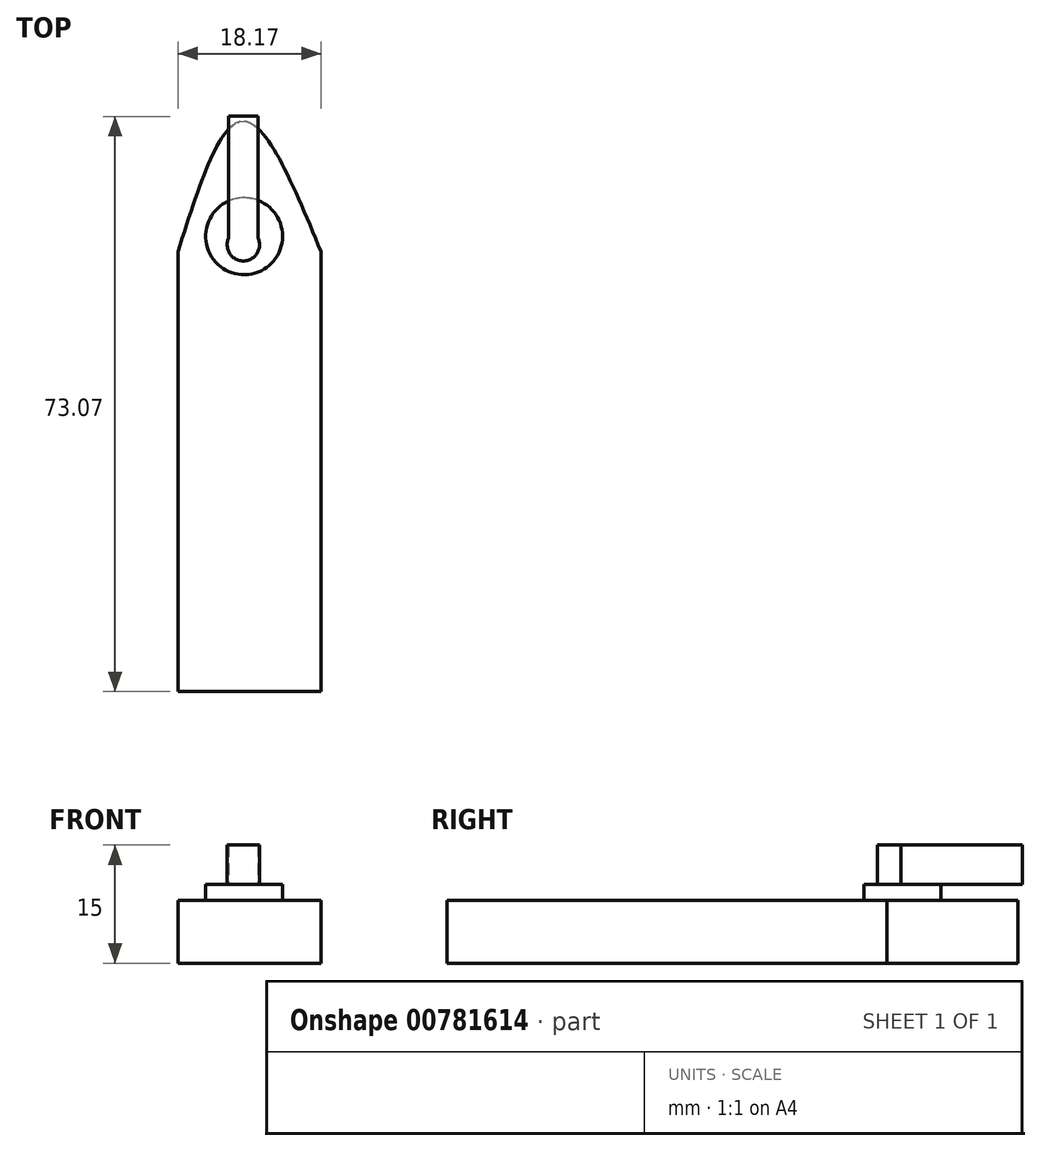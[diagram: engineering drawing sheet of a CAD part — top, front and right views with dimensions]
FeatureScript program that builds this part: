
annotation { "Feature Type Name" : "Feature", "Feature Type Description" : "" }
export const myFeature = defineFeature(function(context is Context, id is Id, definition is map)
    precondition{}
    {
        {
            var Q0;
            Q0=qCreatedBy(makeId("Top.planeOp"),FACE);
            var sketch = newSketch(context, id + "F0", { "sketchPlane" : qUnion([Q0])});
            skLineSegment(sketch, "E0", {"start": v(-36.83, -32.63) * mm, "end": v(-36.83, 23.25) * mm});
            skLineSegment(sketch, "E1", {"start": v(-36.83, 23.25) * mm, "end": v(-18.66, 23.25) * mm});
            skLineSegment(sketch, "E2", {"start": v(-18.66, 23.25) * mm, "end": v(-18.66, -32.63) * mm});
            skLineSegment(sketch, "E3", {"start": v(-18.66, -32.63) * mm, "end": v(-36.83, -32.63) * mm});
            skFitSpline(sketch, "E4", {"points": [v(-36.83, 23.25) * mm, v(-28.62, 39.86) * mm, v(-18.66, 23.25) * mm], "startDerivative": vector(15.83, 50.01) * mm, "endDerivative": vector(20.5, -49.64) * mm});
            skSolve(sketch);
        }
        {
            var Q0;
            Q0 = qSketchRegion(id + "F0", true);
            extrude(context, id + "F1", {"entities" : qUnion([Q0]), "depth" : 8 * mm, "offsetDistance" : 25.4 * mm});
        }
        {
            var Q0;
            Q0=makeQuery(id+"F1.opExtrude","CAP_FACE",FACE,{"disambiguationData":[OSD([sQuery(id+"F0.wireOp",EDGE,"E0"),sQuery(id+"F0.wireOp",EDGE,"E2"),sQuery(id+"F0.wireOp",EDGE,"E3"),sQuery(id+"F0.wireOp",EDGE,"E4")])],"isStart":false});
            var sketch = newSketch(context, id + "F2", { "sketchPlane" : qUnion([Q0])});
            skCircle(sketch, "E5", {"center": v(-28.43, 25.2) * mm, "radius": 4.89 * mm});
            skSolve(sketch);
        }
        {
            var Q0;
            Q0=makeQuery(id+"F2.imprint","IMPRINT",FACE,{"disambiguationData":[TD([[makeQuery(id+"F2.imprint","IMPRINT",EDGE,{"derivedFrom":sQuery(id+"F2.wireOp",EDGE,"E5")}),1.0]])]});
            extrude(context, id + "F3", {"entities" : qUnion([Q0]), "operationType" : NewBodyOperationType.ADD, "depth" : 2 * mm, "offsetDistance" : 25.4 * mm});
        }
        {
            var Q0;
            Q0=makeQuery(id+"F3.opExtrude","CAP_FACE",FACE,{"disambiguationData":[OSD([sQuery(id+"F2.wireOp",EDGE,"E5")])],"isStart":false});
            var sketch = newSketch(context, id + "F4", { "sketchPlane" : qUnion([Q0])});
            skLineSegment(sketch, "E6", {"start": v(-30.38, 25) * mm, "end": v(-30.38, 40.44) * mm});
            skLineSegment(sketch, "E7", {"start": v(-30.38, 25) * mm, "end": v(-26.67, 25) * mm});
            skLineSegment(sketch, "E8", {"start": v(-26.67, 25) * mm, "end": v(-26.67, 40.44) * mm});
            skLineSegment(sketch, "E9", {"start": v(-30.38, 40.44) * mm, "end": v(-26.67, 40.44) * mm});
            skArc(sketch, "E10", {"start": v(-30.38, 25) * mm, "mid": v(-28.53, 22.08) * mm, "end": v(-26.67, 25) * mm});
            skSolve(sketch);
        }
        {
            var Q0;
            Q0 = qSketchRegion(id + "F4", true);
            extrude(context, id + "F5", {"entities" : qUnion([Q0]), "operationType" : NewBodyOperationType.ADD, "depth" : 5 * mm, "offsetDistance" : 25.4 * mm});
        }
    });
